# Revit family: BE_33059_de_DE
name_source: partatom
category: Leuchten
revit_build: Autodesk Revit 2015 (Build: 20150704_0715(x64)
units: mm (PartAtom-declared; Revit-internal decimal feet)

## types (4) — shared parameters
AC/DC = AC/DC
Aktualisierung = 2015-10-30T04:09:34
BEGA_Dummy = Nein
BEGA_IES = Ja
BEGA_Intern = Ja
BEGA_Intern_Konstruktion = Ja
BEGA_Intern_an = Ja
BEGA_Intern_aus = Ja
Beschreibung = Einbauleuchte
Beschreibung_Sonderanfertigung = Hier können Sie Informationen zur Sonderanfertigung eintragen.
Bestellnummer_Einbaugehäuse = ---
CE_Konformität = ja
Einbaugehäuse = Nein
Einbautiefe = 90 mm
Einbauöffnung = 405 x 110 mm
Energieeffizienzklasse = LED A++ - A
Farbfilter = 16777215
Farbtemperaturverschiebung bei Dämpfen der Lampe = <Keine Auswahl>
Farbwiedergabeindex = Ra > 80
Frequenz = 0/50-60 Hz
Gewicht = 2.45 kg
Hersteller = BEGA
Lampe = LED 16.8 W
Lampenlichtstrom = 2260 lm
Lastklassifizierung = Beleuchtung
Lebensdauerkriterien = L70 = 50.000 h
Leuchtenlichtstrom = 1487 lm
Logo = BEGA_Logo.png
Material_02 = BEGA_Oberfläche_Silber_matt
Material_06 = BEGA_Oberfläche_Edelstahl_gebürstet
Material_09 = BEGA_Glas_klar
Material_15 = BEGA_Leuchtmedium_matt
Material_17 = BEGA_Reflektor
Neigungswinkel = 0.00°
Produktdatenblatt = http://www.bega.de
Scheinlast = 0 VA
Schutzart = IP 65
Schutzklasse = I
Sonderanfertigung = Nein
Spannung = 0 V
Typenbild = 33059.png
URL = http://www.bega.de
Umgebungstemperatur = 25 °C
zero-valued in all types: Vorgabe-Ansicht

## per-type parameters (varying)
| type | Bestellnummer | Datei für fotometrisches Netz | Farbtemperatur | LED_Modulbezeichnung | M_A | M_G | Modell |
| BEGA_33059_Grafit_K4 | 33059K4 | BE_33059K4.IES | 4000 K | LED-0573/840 | Nein | Ja | 33059K4 |
| BEGA_33059_Silber_K4 | 33059AK4 | BE_33059K4.IES | 4000 K | LED-0573/840 | Ja | Nein | 33059AK4 |
| BEGA_33059_Grafit_K3 | 33059 | BE_33059.IES | 3000 K | LED-0573/830 | Nein | Ja | 33059 |
| BEGA_33059_Silber_K3 | 33059A | BE_33059.IES | 3000 K | LED-0573/830 | Ja | Nein | 33059A |
